# Revit family: Legrand_Transformateur_IP21_pour_locaux_hospitalier_monophasé
name_source: partatom
category: Installations électriques
revit_build: Autodesk Revit 2018 (Build: 20170223_1515(x64)
units: mm (PartAtom-declared; Revit-internal decimal feet)

## family parameters
Basée sur le plan de construction = Non
Conserver l'orientation des annotations = Non
Cote de connecteur circulaire = Utiliser le diamètre
Couper avec des vides une fois chargée = Non
Numéro OmniClass = 23.80.00.00
Partagée = Non
Point de calcul de pièce = Non
Titre OmniClass = Electric Power and Lighting
Toujours verticalement = Oui
Type d'élément = Normal

## types (6) — shared parameters
Caractéristique = Classe I - IP21 - IK08
Conditions Générale d'Utilisation = https://export.legrand.com
Fabricant = Legrand
Tension primaire = 230V
Tension secondaire = 230V
Type de transformateur = Monophasé 230V/230V point milieu
URL = www.legrand.com
diamètre de fixation = 9 mm  [stored 0.0295276 ft]

## per-type parameters (varying)
| type | 042571 | 042572, 042573, 042574 | 142575, 142576 | Isolant | Poids | Section câble primaire | Section câble secondaire | Ucc (%) | dimension A | dimension B | dimension C | fixation F | fixation G | perte totale max | perte à vide | puissance |
| Transformateur pour locaux hospitaliers 142575 | Non | Non | Oui | classe H | 68.00 kg | 35 mm² | 35 mm² | 3.8 | 390 mm  [stored 1.27953 ft] | 460 mm  [stored 1.50919 ft] | 380 mm | 370 mm  [stored 1.21391 ft] | 140 mm  [stored 0.459318 ft] | 470 W | 88 W | 8 kVA |
| Transformateur pour locaux hospitaliers 142576 | Non | Non | Oui | classe H | 70.00 kg | 35 mm² | 35 mm² | 3.6 | 390 mm  [stored 1.27953 ft] | 460 mm  [stored 1.50919 ft] | 380 mm | 370 mm  [stored 1.21391 ft] | 140 mm  [stored 0.459318 ft] | 486 W | 90 W | 10 kVA |
| Transformateur pour locaux hospitaliers 042571 | Oui | Non | Non | classe B | 39.00 kg | 16 mm² | 16 mm² | 3.1 | 320 mm  [stored 1.04987 ft] | 330 mm  [stored 1.08268 ft] | 253 mm  [stored 0.830052 ft] | 300 mm  [stored 0.984252 ft] | 111 mm | 115 W | 22 W | 3 kVA |
| Transformateur pour locaux hospitaliers 042572 | Non | Oui | Non | classe H | 52.00 kg | 16 mm² | 16 mm² | 3.2 | 340 mm  [stored 1.11549 ft] | 410 mm  [stored 1.34514 ft] | 370 mm  [stored 1.21391 ft] | 320 mm  [stored 1.04987 ft] | 120 mm  [stored 0.393701 ft] | 228 W | 46 W | 4 kVA |
| Transformateur pour locaux hospitaliers 042573 | Non | Oui | Non | classe H | 60.00 kg | 35 mm² | 35 mm² | 3.1 | 340 mm  [stored 1.11549 ft] | 410 mm  [stored 1.34514 ft] | 370 mm  [stored 1.21391 ft] | 320 mm  [stored 1.04987 ft] | 150 mm | 305 W | 64 W | 5 kVA |
| Transformateur pour locaux hospitaliers 042574 | Non | Oui | Non | classe H | 68.00 kg | 35 mm² | 35 mm² | 2.8 | 340 mm  [stored 1.11549 ft] | 410 mm  [stored 1.34514 ft] | 370 mm  [stored 1.21391 ft] | 320 mm  [stored 1.04987 ft] | 150 mm | 281 W | 68 W | 6 kVA |

note: [stored X ft] marks values corroborated as IEEE doubles in the binary element streams (Revit-internal decimal feet)
